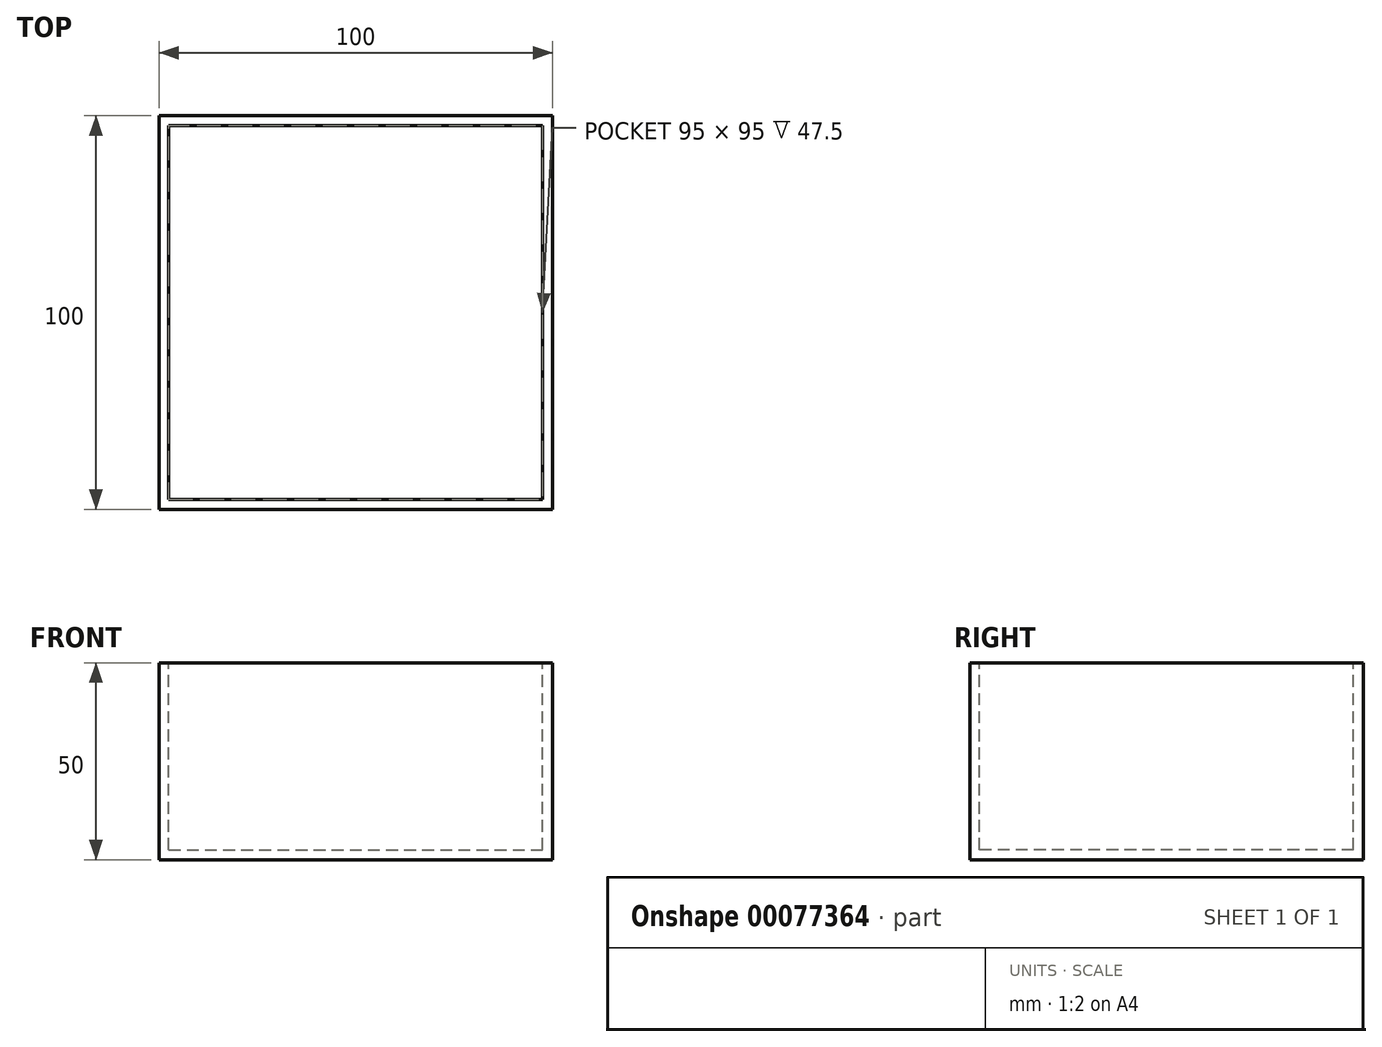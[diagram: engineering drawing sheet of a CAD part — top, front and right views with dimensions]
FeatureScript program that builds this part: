
annotation { "Feature Type Name" : "Feature", "Feature Type Description" : "" }
export const myFeature = defineFeature(function(context is Context, id is Id, definition is map)
    precondition{}
    {
        {
            var Q0;
            Q0=qCreatedBy(makeId("Front.planeOp"),FACE);
            var sketch = newSketch(context, id + "F0", { "sketchPlane" : qUnion([Q0])});
            skLineSegment(sketch, "E0.bottom", {"start": v(0, 0) * mm, "end": v(100, 0) * mm});
            skLineSegment(sketch, "E0.top", {"start": v(0, 50) * mm, "end": v(100, 50) * mm});
            skLineSegment(sketch, "E0.left", {"start": v(0, 0) * mm, "end": v(0, 50) * mm});
            skLineSegment(sketch, "E0.right", {"start": v(100, 0) * mm, "end": v(100, 50) * mm});
            skSolve(sketch);
        }
        {
            var Q0;
            Q0 = qSketchRegion(id + "F0", true);
            extrude(context, id + "F1", {"entities" : qUnion([Q0]), "oppositeDirection" : true, "depth" : 100 * mm});
        }
        {
            var Q0;
            Q0=makeQuery(id+"F1.opExtrude","SWEPT_FACE",FACE,{"disambiguationData":[OSD([sQuery(id+"F0.wireOp",EDGE,"E0.top")])]});
            shell(context, id + "F2", {"entities" : qUnion([Q0]), "thickness" : 2.5 * mm});
        }
    });
